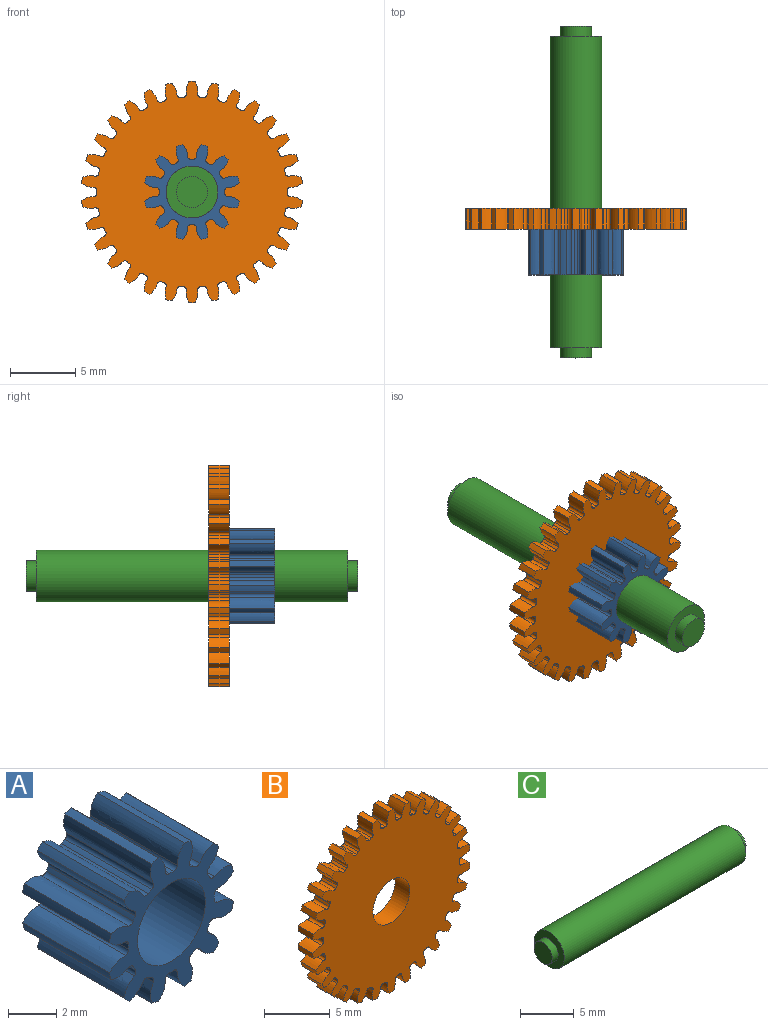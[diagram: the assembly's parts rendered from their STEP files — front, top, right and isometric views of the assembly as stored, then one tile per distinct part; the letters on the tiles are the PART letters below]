
ASSEMBLY  parts=3 mates=2
PART A: 75 faces, bbox 7.3x5.1x7.3 mm
  f0: extruded ~5.08x0.93mm, area 5.4mm2, adj f47,f48,f49,f50
  f1: cylinder r=2.51mm len=5.08mm, axis (0,1,0), area 1.2mm2, adj f48,f49,f50,f51
  f2: extruded ~5.08x0.93mm, area 5.4mm2, adj f3,f48,f49,f51
  f3: cylinder r=3.7mm len=5.08mm, axis (0,1,0), area 2.1mm2, adj f2,f4,f48,f49
  f4: extruded ~5.08x1.01mm, area 5.4mm2, adj f3,f48,f49,f52
  f5: cylinder r=2.51mm len=5.08mm, axis (0,1,0), area 1.2mm2, adj f48,f49,f52,f53
  f6: extruded ~5.08x0.82mm, area 5.4mm2, adj f7,f48,f49,f53
  f7: cylinder r=3.7mm len=5.08mm, axis (0,1,0), area 2.1mm2, adj f6,f8,f48,f49
  f8: extruded ~5.08x0.82mm, area 5.4mm2, adj f7,f48,f49,f54
  f9: cylinder r=2.51mm len=5.08mm, axis (0,1,0), area 1.2mm2, adj f48,f49,f54,f55
  f10: extruded ~5.08x1.01mm, area 5.4mm2, adj f11,f48,f49,f55
  f11: cylinder r=3.7mm len=5.08mm, axis (0,1,0), area 2.1mm2, adj f10,f12,f48,f49
  f12: extruded ~5.08x0.93mm, area 5.4mm2, adj f11,f48,f49,f56
  f13: cylinder r=2.51mm len=5.08mm, axis (0,1,0), area 1.2mm2, adj f48,f49,f56,f57
  f14: extruded ~5.08x0.93mm, area 5.4mm2, adj f15,f48,f49,f57
  f15: cylinder r=3.7mm len=5.08mm, axis (0,1,0), area 2.1mm2, adj f14,f16,f48,f49
  f16: extruded ~5.08x1.01mm, area 5.4mm2, adj f15,f48,f49,f58
  f17: cylinder r=2.51mm len=5.08mm, axis (0,1,0), area 1.2mm2, adj f48,f49,f58,f59
  f18: extruded ~5.08x0.82mm, area 5.4mm2, adj f19,f48,f49,f59
  f19: cylinder r=3.7mm len=5.08mm, axis (0,1,0), area 2.1mm2, adj f18,f20,f48,f49
  f20: extruded ~5.08x0.82mm, area 5.4mm2, adj f19,f48,f49,f60
  f21: cylinder r=2.51mm len=5.08mm, axis (0,1,0), area 1.2mm2, adj f48,f49,f60,f61
  f22: extruded ~5.08x1.01mm, area 5.4mm2, adj f23,f48,f49,f61
  f23: cylinder r=3.7mm len=5.08mm, axis (0,1,0), area 2.1mm2, adj f22,f24,f48,f49
  f24: extruded ~5.08x0.93mm, area 5.4mm2, adj f23,f48,f49,f62
  f25: cylinder r=2.51mm len=5.08mm, axis (0,1,0), area 1.2mm2, adj f48,f49,f62,f63
  f26: extruded ~5.08x0.93mm, area 5.4mm2, adj f27,f48,f49,f63
  f27: cylinder r=3.7mm len=5.08mm, axis (0,1,0), area 2.1mm2, adj f26,f28,f48,f49
  f28: extruded ~5.08x1.01mm, area 5.4mm2, adj f27,f48,f49,f64
  f29: cylinder r=2.51mm len=5.08mm, axis (0,1,0), area 1.2mm2, adj f48,f49,f64,f65
  f30: extruded ~5.08x0.82mm, area 5.4mm2, adj f31,f48,f49,f65
  f31: cylinder r=3.7mm len=5.08mm, axis (0,1,0), area 2.1mm2, adj f30,f32,f48,f49
  f32: extruded ~5.08x0.82mm, area 5.4mm2, adj f31,f48,f49,f66
  f33: cylinder r=2.51mm len=5.08mm, axis (0,1,0), area 1.2mm2, adj f48,f49,f66,f67
  f34: extruded ~5.08x1.01mm, area 5.4mm2, adj f35,f48,f49,f67
  f35: cylinder r=3.7mm len=5.08mm, axis (0,1,0), area 2.1mm2, adj f34,f36,f48,f49
  f36: extruded ~5.08x0.93mm, area 5.4mm2, adj f35,f48,f49,f68
  f37: cylinder r=2.51mm len=5.08mm, axis (0,1,0), area 1.2mm2, adj f48,f49,f68,f69
  f38: extruded ~5.08x0.93mm, area 5.4mm2, adj f39,f48,f49,f69
  f39: cylinder r=3.7mm len=5.08mm, axis (0,1,0), area 2.1mm2, adj f38,f40,f48,f49
  f40: extruded ~5.08x1.01mm, area 5.4mm2, adj f39,f48,f49,f70
  f41: cylinder r=2.51mm len=5.08mm, axis (0,1,0), area 1.2mm2, adj f48,f49,f70,f71
  f42: extruded ~5.08x0.82mm, area 5.4mm2, adj f43,f48,f49,f71
  f43: cylinder r=3.7mm len=5.08mm, axis (0,1,0), area 2.1mm2, adj f42,f44,f48,f49
  f44: extruded ~5.08x0.82mm, area 5.4mm2, adj f43,f48,f49,f72
  f45: cylinder r=2.51mm len=5.08mm, axis (0,1,0), area 1.2mm2, adj f48,f49,f72,f73
  f46: extruded ~5.08x1.01mm, area 5.4mm2, adj f47,f48,f49,f73
  f47: cylinder r=3.7mm len=5.08mm, axis (0,1,0), area 2.1mm2, adj f0,f46,f48,f49
  f48: plane 7.28x7.28mm, normal (0,-1,0), area 18.1mm2, adj f0,f1,f2,f3,f4,f5,f6,f7
  f49: plane 7.28x7.28mm, normal (0,1,0), area 18.1mm2, adj f0,f1,f2,f3,f4,f5,f6,f7
  f50: cylinder r=0.21mm len=5.08mm, axis (0,1,0), area 1.6mm2, adj f0,f1,f48,f49
  f51: cylinder r=0.21mm len=5.08mm, axis (0,1,0), area 1.6mm2, adj f1,f2,f48,f49
  f52: cylinder r=0.21mm len=5.08mm, axis (0,1,0), area 1.6mm2, adj f4,f5,f48,f49
  f53: cylinder r=0.21mm len=5.08mm, axis (0,1,0), area 1.6mm2, adj f5,f6,f48,f49
  f54: cylinder r=0.21mm len=5.08mm, axis (0,1,0), area 1.6mm2, adj f8,f9,f48,f49
  f55: cylinder r=0.21mm len=5.08mm, axis (0,1,0), area 1.6mm2, adj f9,f10,f48,f49
  f56: cylinder r=0.21mm len=5.08mm, axis (0,1,0), area 1.6mm2, adj f12,f13,f48,f49
  f57: cylinder r=0.21mm len=5.08mm, axis (0,1,0), area 1.6mm2, adj f13,f14,f48,f49
  f58: cylinder r=0.21mm len=5.08mm, axis (0,1,0), area 1.6mm2, adj f16,f17,f48,f49
  f59: cylinder r=0.21mm len=5.08mm, axis (0,1,0), area 1.6mm2, adj f17,f18,f48,f49
  f60: cylinder r=0.21mm len=5.08mm, axis (0,1,0), area 1.6mm2, adj f20,f21,f48,f49
  f61: cylinder r=0.21mm len=5.08mm, axis (0,1,0), area 1.6mm2, adj f21,f22,f48,f49
  f62: cylinder r=0.21mm len=5.08mm, axis (0,1,0), area 1.6mm2, adj f24,f25,f48,f49
  f63: cylinder r=0.21mm len=5.08mm, axis (0,1,0), area 1.6mm2, adj f25,f26,f48,f49
  f64: cylinder r=0.21mm len=5.08mm, axis (0,1,0), area 1.6mm2, adj f28,f29,f48,f49
  f65: cylinder r=0.21mm len=5.08mm, axis (0,1,0), area 1.6mm2, adj f29,f30,f48,f49
  f66: cylinder r=0.21mm len=5.08mm, axis (0,1,0), area 1.6mm2, adj f32,f33,f48,f49
  f67: cylinder r=0.21mm len=5.08mm, axis (0,1,0), area 1.6mm2, adj f33,f34,f48,f49
  f68: cylinder r=0.21mm len=5.08mm, axis (0,1,0), area 1.6mm2, adj f36,f37,f48,f49
  f69: cylinder r=0.21mm len=5.08mm, axis (0,1,0), area 1.6mm2, adj f37,f38,f48,f49
  f70: cylinder r=0.21mm len=5.08mm, axis (0,1,0), area 1.6mm2, adj f40,f41,f48,f49
  f71: cylinder r=0.21mm len=5.08mm, axis (0,1,0), area 1.6mm2, adj f41,f42,f48,f49
  f72: cylinder r=0.21mm len=5.08mm, axis (0,1,0), area 1.6mm2, adj f44,f45,f48,f49
  f73: cylinder r=0.21mm len=5.08mm, axis (0,1,0), area 1.6mm2, adj f45,f46,f48,f49
  f74: cylinder r=1.98mm len=5.08mm, axis (0,1,0), area 63.3mm2, adj f48,f49
PART B: 183 faces, bbox 16.9x1.6x16.9 mm
  f0: extruded ~1.59x0.95mm, area 1.6mm2, adj f120,f121,f122,f123
  f1: cylinder r=7.28mm len=1.59mm, axis (0,1,0), area 0.4mm2, adj f121,f122,f123,f124
  f2: extruded ~1.59x0.95mm, area 1.6mm2, adj f3,f121,f122,f124
  f3: cylinder r=8.47mm len=1.59mm, axis (0,1,0), area 0.8mm2, adj f2,f4,f121,f122
  f4: extruded ~1.59x0.99mm, area 1.6mm2, adj f3,f121,f122,f125
  f5: cylinder r=7.28mm len=1.59mm, axis (0,1,0), area 0.4mm2, adj f121,f122,f125,f126
  f6: extruded ~1.59x0.87mm, area 1.6mm2, adj f7,f121,f122,f126
  f7: cylinder r=8.47mm len=1.59mm, axis (0,1,0), area 0.8mm2, adj f6,f8,f121,f122
  f8: extruded ~1.59x0.98mm, area 1.6mm2, adj f7,f121,f122,f127
  f9: cylinder r=7.28mm len=1.59mm, axis (0,1,0), area 0.4mm2, adj f121,f122,f127,f128
  f10: extruded ~1.59x0.75mm, area 1.6mm2, adj f11,f121,f122,f128
  f11: cylinder r=8.47mm len=1.59mm, axis (0,1,0), area 0.8mm2, adj f10,f12,f121,f122
  f12: extruded ~1.59x0.94mm, area 1.6mm2, adj f11,f121,f122,f129
  f13: cylinder r=7.28mm len=1.59mm, axis (0,1,0), area 0.4mm2, adj f121,f122,f129,f130
  f14: extruded ~1.59x0.79mm, area 1.6mm2, adj f15,f121,f122,f130
  f15: cylinder r=8.47mm len=1.59mm, axis (0,1,0), area 0.8mm2, adj f14,f16,f121,f122
  f16: extruded ~1.59x0.85mm, area 1.6mm2, adj f15,f121,f122,f131
  f17: cylinder r=7.28mm len=1.59mm, axis (0,1,0), area 0.4mm2, adj f121,f122,f131,f132
  f18: extruded ~1.59x0.9mm, area 1.6mm2, adj f19,f121,f122,f132
  f19: cylinder r=8.47mm len=1.59mm, axis (0,1,0), area 0.8mm2, adj f18,f20,f121,f122
  f20: extruded ~1.59x0.72mm, area 1.6mm2, adj f19,f121,f122,f133
  f21: cylinder r=7.28mm len=1.59mm, axis (0,1,0), area 0.4mm2, adj f121,f122,f133,f134
  f22: extruded ~1.59x0.96mm, area 1.6mm2, adj f23,f121,f122,f134
  f23: cylinder r=8.47mm len=1.59mm, axis (0,1,0), area 0.8mm2, adj f22,f24,f121,f122
  f24: extruded ~1.59x0.81mm, area 1.6mm2, adj f23,f121,f122,f135
  f25: cylinder r=7.28mm len=1.59mm, axis (0,1,0), area 0.4mm2, adj f121,f122,f135,f136
  f26: extruded ~1.59x0.99mm, area 1.6mm2, adj f27,f121,f122,f136
  f27: cylinder r=8.47mm len=1.59mm, axis (0,1,0), area 0.8mm2, adj f26,f28,f121,f122
  f28: extruded ~1.59x0.91mm, area 1.6mm2, adj f27,f121,f122,f137
  f29: cylinder r=7.28mm len=1.59mm, axis (0,1,0), area 0.4mm2, adj f121,f122,f137,f138
  f30: extruded ~1.59x0.97mm, area 1.6mm2, adj f31,f121,f122,f138
  f31: cylinder r=8.47mm len=1.59mm, axis (0,1,0), area 0.8mm2, adj f30,f32,f121,f122
  f32: extruded ~1.59x0.97mm, area 1.6mm2, adj f31,f121,f122,f139
  f33: cylinder r=7.28mm len=1.59mm, axis (0,1,0), area 0.4mm2, adj f121,f122,f139,f140
  f34: extruded ~1.59x0.91mm, area 1.6mm2, adj f35,f121,f122,f140
  f35: cylinder r=8.47mm len=1.59mm, axis (0,1,0), area 0.8mm2, adj f34,f36,f121,f122
  f36: extruded ~1.59x0.99mm, area 1.6mm2, adj f35,f121,f122,f141
  f37: cylinder r=7.28mm len=1.59mm, axis (0,1,0), area 0.4mm2, adj f121,f122,f141,f142
  f38: extruded ~1.59x0.81mm, area 1.6mm2, adj f39,f121,f122,f142
  f39: cylinder r=8.47mm len=1.59mm, axis (0,1,0), area 0.8mm2, adj f38,f40,f121,f122
  f40: extruded ~1.59x0.96mm, area 1.6mm2, adj f39,f121,f122,f143
  f41: cylinder r=7.28mm len=1.59mm, axis (0,1,0), area 0.4mm2, adj f121,f122,f143,f144
  f42: extruded ~1.59x0.72mm, area 1.6mm2, adj f43,f121,f122,f144
  f43: cylinder r=8.47mm len=1.59mm, axis (0,1,0), area 0.8mm2, adj f42,f44,f121,f122
  f44: extruded ~1.59x0.9mm, area 1.6mm2, adj f43,f121,f122,f145
  f45: cylinder r=7.28mm len=1.59mm, axis (0,1,0), area 0.4mm2, adj f121,f122,f145,f146
  f46: extruded ~1.59x0.85mm, area 1.6mm2, adj f47,f121,f122,f146
  f47: cylinder r=8.47mm len=1.59mm, axis (0,1,0), area 0.8mm2, adj f46,f48,f121,f122
  f48: extruded ~1.59x0.79mm, area 1.6mm2, adj f47,f121,f122,f147
  f49: cylinder r=7.28mm len=1.59mm, axis (0,1,0), area 0.4mm2, adj f121,f122,f147,f148
  f50: extruded ~1.59x0.94mm, area 1.6mm2, adj f51,f121,f122,f148
  f51: cylinder r=8.47mm len=1.59mm, axis (0,1,0), area 0.8mm2, adj f50,f52,f121,f122
  f52: extruded ~1.59x0.75mm, area 1.6mm2, adj f51,f121,f122,f149
  f53: cylinder r=7.28mm len=1.59mm, axis (0,1,0), area 0.4mm2, adj f121,f122,f149,f150
  f54: extruded ~1.59x0.98mm, area 1.6mm2, adj f55,f121,f122,f150
  f55: cylinder r=8.47mm len=1.59mm, axis (0,1,0), area 0.8mm2, adj f54,f56,f121,f122
  f56: extruded ~1.59x0.87mm, area 1.6mm2, adj f55,f121,f122,f151
  f57: cylinder r=7.28mm len=1.59mm, axis (0,1,0), area 0.4mm2, adj f121,f122,f151,f152
  f58: extruded ~1.59x0.99mm, area 1.6mm2, adj f59,f121,f122,f152
  f59: cylinder r=8.47mm len=1.59mm, axis (0,1,0), area 0.8mm2, adj f58,f60,f121,f122
  f60: extruded ~1.59x0.95mm, area 1.6mm2, adj f59,f121,f122,f153
  f61: cylinder r=7.28mm len=1.59mm, axis (0,1,0), area 0.4mm2, adj f121,f122,f153,f154
  f62: extruded ~1.59x0.95mm, area 1.6mm2, adj f63,f121,f122,f154
  f63: cylinder r=8.47mm len=1.59mm, axis (0,1,0), area 0.8mm2, adj f62,f64,f121,f122
  f64: extruded ~1.59x0.99mm, area 1.6mm2, adj f63,f121,f122,f155
  f65: cylinder r=7.28mm len=1.59mm, axis (0,1,0), area 0.4mm2, adj f121,f122,f155,f156
  f66: extruded ~1.59x0.87mm, area 1.6mm2, adj f67,f121,f122,f156
  f67: cylinder r=8.47mm len=1.59mm, axis (0,1,0), area 0.8mm2, adj f66,f68,f121,f122
  f68: extruded ~1.59x0.98mm, area 1.6mm2, adj f67,f121,f122,f157
  f69: cylinder r=7.28mm len=1.59mm, axis (0,1,0), area 0.4mm2, adj f121,f122,f157,f158
  f70: extruded ~1.59x0.75mm, area 1.6mm2, adj f71,f121,f122,f158
  f71: cylinder r=8.47mm len=1.59mm, axis (0,1,0), area 0.8mm2, adj f70,f72,f121,f122
  f72: extruded ~1.59x0.94mm, area 1.6mm2, adj f71,f121,f122,f159
  f73: cylinder r=7.28mm len=1.59mm, axis (0,1,0), area 0.4mm2, adj f121,f122,f159,f160
  f74: extruded ~1.59x0.79mm, area 1.6mm2, adj f75,f121,f122,f160
  f75: cylinder r=8.47mm len=1.59mm, axis (0,1,0), area 0.8mm2, adj f74,f76,f121,f122
  f76: extruded ~1.59x0.85mm, area 1.6mm2, adj f75,f121,f122,f161
  f77: cylinder r=7.28mm len=1.59mm, axis (0,1,0), area 0.4mm2, adj f121,f122,f161,f162
  f78: extruded ~1.59x0.9mm, area 1.6mm2, adj f79,f121,f122,f162
  f79: cylinder r=8.47mm len=1.59mm, axis (0,1,0), area 0.8mm2, adj f78,f80,f121,f122
  f80: extruded ~1.59x0.72mm, area 1.6mm2, adj f79,f121,f122,f163
  f81: cylinder r=7.28mm len=1.59mm, axis (0,1,0), area 0.4mm2, adj f121,f122,f163,f164
  f82: extruded ~1.59x0.96mm, area 1.6mm2, adj f83,f121,f122,f164
  f83: cylinder r=8.47mm len=1.59mm, axis (0,1,0), area 0.8mm2, adj f82,f84,f121,f122
  f84: extruded ~1.59x0.81mm, area 1.6mm2, adj f83,f121,f122,f165
  f85: cylinder r=7.28mm len=1.59mm, axis (0,1,0), area 0.4mm2, adj f121,f122,f165,f166
  f86: extruded ~1.59x0.99mm, area 1.6mm2, adj f87,f121,f122,f166
  f87: cylinder r=8.47mm len=1.59mm, axis (0,1,0), area 0.8mm2, adj f86,f88,f121,f122
  f88: extruded ~1.59x0.91mm, area 1.6mm2, adj f87,f121,f122,f167
  f89: cylinder r=7.28mm len=1.59mm, axis (0,1,0), area 0.4mm2, adj f121,f122,f167,f168
  f90: extruded ~1.59x0.97mm, area 1.6mm2, adj f91,f121,f122,f168
  f91: cylinder r=8.47mm len=1.59mm, axis (0,1,0), area 0.8mm2, adj f90,f92,f121,f122
  f92: extruded ~1.59x0.97mm, area 1.6mm2, adj f91,f121,f122,f169
  f93: cylinder r=7.28mm len=1.59mm, axis (0,1,0), area 0.4mm2, adj f121,f122,f169,f170
  f94: extruded ~1.59x0.91mm, area 1.6mm2, adj f95,f121,f122,f170
  f95: cylinder r=8.47mm len=1.59mm, axis (0,1,0), area 0.8mm2, adj f94,f96,f121,f122
  f96: extruded ~1.59x0.99mm, area 1.6mm2, adj f95,f121,f122,f171
  f97: cylinder r=7.28mm len=1.59mm, axis (0,1,0), area 0.4mm2, adj f121,f122,f171,f172
  f98: extruded ~1.59x0.81mm, area 1.6mm2, adj f99,f121,f122,f172
  f99: cylinder r=8.47mm len=1.59mm, axis (0,1,0), area 0.8mm2, adj f98,f100,f121,f122
  f100: extruded ~1.59x0.96mm, area 1.6mm2, adj f99,f121,f122,f173
  f101: cylinder r=7.28mm len=1.59mm, axis (0,1,0), area 0.4mm2, adj f121,f122,f173,f174
  f102: extruded ~1.59x0.72mm, area 1.6mm2, adj f103,f121,f122,f174
  f103: cylinder r=8.47mm len=1.59mm, axis (0,1,0), area 0.8mm2, adj f102,f104,f121,f122
  f104: extruded ~1.59x0.9mm, area 1.6mm2, adj f103,f121,f122,f175
  f105: cylinder r=7.28mm len=1.59mm, axis (0,1,0), area 0.4mm2, adj f121,f122,f175,f176
  f106: extruded ~1.59x0.85mm, area 1.6mm2, adj f107,f121,f122,f176
  f107: cylinder r=8.47mm len=1.59mm, axis (0,1,0), area 0.8mm2, adj f106,f108,f121,f122
  f108: extruded ~1.59x0.79mm, area 1.6mm2, adj f107,f121,f122,f177
  f109: cylinder r=7.28mm len=1.59mm, axis (0,1,0), area 0.4mm2, adj f121,f122,f177,f178
  f110: extruded ~1.59x0.94mm, area 1.6mm2, adj f111,f121,f122,f178
  f111: cylinder r=8.47mm len=1.59mm, axis (0,1,0), area 0.8mm2, adj f110,f112,f121,f122
  f112: extruded ~1.59x0.75mm, area 1.6mm2, adj f111,f121,f122,f179
  f113: cylinder r=7.28mm len=1.59mm, axis (0,1,0), area 0.4mm2, adj f121,f122,f179,f180
  f114: extruded ~1.59x0.98mm, area 1.6mm2, adj f115,f121,f122,f180
  f115: cylinder r=8.47mm len=1.59mm, axis (0,1,0), area 0.8mm2, adj f114,f116,f121,f122
  f116: extruded ~1.59x0.87mm, area 1.6mm2, adj f115,f121,f122,f181
  f117: cylinder r=7.28mm len=1.59mm, axis (0,1,0), area 0.4mm2, adj f121,f122,f181,f182
  f118: extruded ~1.59x0.99mm, area 1.6mm2, adj f120,f121,f122,f182
  f119: cylinder r=1.98mm len=3.97mm, axis (0,1,0), area 19.8mm2, adj f121,f122
  f120: cylinder r=8.47mm len=1.59mm, axis (0,1,0), area 0.8mm2, adj f0,f118,f121,f122
  f121: plane 16.94x16.9mm, normal (0,-1,0), area 182.5mm2, adj f0,f1,f2,f3,f4,f5,f6,f7
  f122: plane 16.94x16.9mm, normal (0,1,0), area 182.5mm2, adj f0,f1,f2,f3,f4,f5,f6,f7
  f123: cylinder r=0.23mm len=1.59mm, axis (0,1,0), area 0.6mm2, adj f0,f1,f121,f122
  f124: cylinder r=0.23mm len=1.59mm, axis (0,1,0), area 0.6mm2, adj f1,f2,f121,f122
  f125: cylinder r=0.23mm len=1.59mm, axis (0,1,0), area 0.6mm2, adj f4,f5,f121,f122
  f126: cylinder r=0.23mm len=1.59mm, axis (0,1,0), area 0.6mm2, adj f5,f6,f121,f122
  f127: cylinder r=0.23mm len=1.59mm, axis (0,1,0), area 0.6mm2, adj f8,f9,f121,f122
  f128: cylinder r=0.23mm len=1.59mm, axis (0,1,0), area 0.6mm2, adj f9,f10,f121,f122
  f129: cylinder r=0.23mm len=1.59mm, axis (0,1,0), area 0.6mm2, adj f12,f13,f121,f122
  f130: cylinder r=0.23mm len=1.59mm, axis (0,1,0), area 0.6mm2, adj f13,f14,f121,f122
  f131: cylinder r=0.23mm len=1.59mm, axis (0,1,0), area 0.6mm2, adj f16,f17,f121,f122
  f132: cylinder r=0.23mm len=1.59mm, axis (0,1,0), area 0.6mm2, adj f17,f18,f121,f122
  f133: cylinder r=0.23mm len=1.59mm, axis (0,1,0), area 0.6mm2, adj f20,f21,f121,f122
  f134: cylinder r=0.23mm len=1.59mm, axis (0,1,0), area 0.6mm2, adj f21,f22,f121,f122
  f135: cylinder r=0.23mm len=1.59mm, axis (0,1,0), area 0.6mm2, adj f24,f25,f121,f122
  f136: cylinder r=0.23mm len=1.59mm, axis (0,1,0), area 0.6mm2, adj f25,f26,f121,f122
  f137: cylinder r=0.23mm len=1.59mm, axis (0,1,0), area 0.6mm2, adj f28,f29,f121,f122
  f138: cylinder r=0.23mm len=1.59mm, axis (0,1,0), area 0.6mm2, adj f29,f30,f121,f122
  f139: cylinder r=0.23mm len=1.59mm, axis (0,1,0), area 0.6mm2, adj f32,f33,f121,f122
  f140: cylinder r=0.23mm len=1.59mm, axis (0,1,0), area 0.6mm2, adj f33,f34,f121,f122
  f141: cylinder r=0.23mm len=1.59mm, axis (0,1,0), area 0.6mm2, adj f36,f37,f121,f122
  f142: cylinder r=0.23mm len=1.59mm, axis (0,1,0), area 0.6mm2, adj f37,f38,f121,f122
  f143: cylinder r=0.23mm len=1.59mm, axis (0,1,0), area 0.6mm2, adj f40,f41,f121,f122
  f144: cylinder r=0.23mm len=1.59mm, axis (0,1,0), area 0.6mm2, adj f41,f42,f121,f122
  f145: cylinder r=0.23mm len=1.59mm, axis (0,1,0), area 0.6mm2, adj f44,f45,f121,f122
  f146: cylinder r=0.23mm len=1.59mm, axis (0,1,0), area 0.6mm2, adj f45,f46,f121,f122
  f147: cylinder r=0.23mm len=1.59mm, axis (0,1,0), area 0.6mm2, adj f48,f49,f121,f122
  f148: cylinder r=0.23mm len=1.59mm, axis (0,1,0), area 0.6mm2, adj f49,f50,f121,f122
  f149: cylinder r=0.23mm len=1.59mm, axis (0,1,0), area 0.6mm2, adj f52,f53,f121,f122
  f150: cylinder r=0.23mm len=1.59mm, axis (0,1,0), area 0.6mm2, adj f53,f54,f121,f122
  f151: cylinder r=0.23mm len=1.59mm, axis (0,1,0), area 0.6mm2, adj f56,f57,f121,f122
  f152: cylinder r=0.23mm len=1.59mm, axis (0,1,0), area 0.6mm2, adj f57,f58,f121,f122
  f153: cylinder r=0.23mm len=1.59mm, axis (0,1,0), area 0.6mm2, adj f60,f61,f121,f122
  f154: cylinder r=0.23mm len=1.59mm, axis (0,1,0), area 0.6mm2, adj f61,f62,f121,f122
  f155: cylinder r=0.23mm len=1.59mm, axis (0,1,0), area 0.6mm2, adj f64,f65,f121,f122
  f156: cylinder r=0.23mm len=1.59mm, axis (0,1,0), area 0.6mm2, adj f65,f66,f121,f122
  f157: cylinder r=0.23mm len=1.59mm, axis (0,1,0), area 0.6mm2, adj f68,f69,f121,f122
  f158: cylinder r=0.23mm len=1.59mm, axis (0,1,0), area 0.6mm2, adj f69,f70,f121,f122
  f159: cylinder r=0.23mm len=1.59mm, axis (0,1,0), area 0.6mm2, adj f72,f73,f121,f122
  f160: cylinder r=0.23mm len=1.59mm, axis (0,1,0), area 0.6mm2, adj f73,f74,f121,f122
  f161: cylinder r=0.23mm len=1.59mm, axis (0,1,0), area 0.6mm2, adj f76,f77,f121,f122
  f162: cylinder r=0.23mm len=1.59mm, axis (0,1,0), area 0.6mm2, adj f77,f78,f121,f122
  f163: cylinder r=0.23mm len=1.59mm, axis (0,1,0), area 0.6mm2, adj f80,f81,f121,f122
  f164: cylinder r=0.23mm len=1.59mm, axis (0,1,0), area 0.6mm2, adj f81,f82,f121,f122
  f165: cylinder r=0.23mm len=1.59mm, axis (0,1,0), area 0.6mm2, adj f84,f85,f121,f122
  f166: cylinder r=0.23mm len=1.59mm, axis (0,1,0), area 0.6mm2, adj f85,f86,f121,f122
  f167: cylinder r=0.23mm len=1.59mm, axis (0,1,0), area 0.6mm2, adj f88,f89,f121,f122
  f168: cylinder r=0.23mm len=1.59mm, axis (0,1,0), area 0.6mm2, adj f89,f90,f121,f122
  f169: cylinder r=0.23mm len=1.59mm, axis (0,1,0), area 0.6mm2, adj f92,f93,f121,f122
  f170: cylinder r=0.23mm len=1.59mm, axis (0,1,0), area 0.6mm2, adj f93,f94,f121,f122
  f171: cylinder r=0.23mm len=1.59mm, axis (0,1,0), area 0.6mm2, adj f96,f97,f121,f122
  f172: cylinder r=0.23mm len=1.59mm, axis (0,1,0), area 0.6mm2, adj f97,f98,f121,f122
  f173: cylinder r=0.23mm len=1.59mm, axis (0,1,0), area 0.6mm2, adj f100,f101,f121,f122
  f174: cylinder r=0.23mm len=1.59mm, axis (0,1,0), area 0.6mm2, adj f101,f102,f121,f122
  f175: cylinder r=0.23mm len=1.59mm, axis (0,1,0), area 0.6mm2, adj f104,f105,f121,f122
  f176: cylinder r=0.23mm len=1.59mm, axis (0,1,0), area 0.6mm2, adj f105,f106,f121,f122
  f177: cylinder r=0.23mm len=1.59mm, axis (0,1,0), area 0.6mm2, adj f108,f109,f121,f122
  f178: cylinder r=0.23mm len=1.59mm, axis (0,1,0), area 0.6mm2, adj f109,f110,f121,f122
  f179: cylinder r=0.23mm len=1.59mm, axis (0,1,0), area 0.6mm2, adj f112,f113,f121,f122
  f180: cylinder r=0.23mm len=1.59mm, axis (0,1,0), area 0.6mm2, adj f113,f114,f121,f122
  f181: cylinder r=0.23mm len=1.59mm, axis (0,1,0), area 0.6mm2, adj f116,f117,f121,f122
  f182: cylinder r=0.23mm len=1.59mm, axis (0,1,0), area 0.6mm2, adj f117,f118,f121,f122
PART C: 7 faces, bbox 25.4x4x4 mm
  f0: cylinder r=1.19mm len=2.38mm, axis (-1,0,0), area 5.9mm2, adj f1,f3
  f1: plane 2.38x2.38mm, normal (1,0,0), area 4.5mm2, adj f0
  f2: cylinder r=1.98mm len=23.81mm, axis (-1,0,0), area 296.9mm2, adj f3,f4
  f3: plane 3.97x3.97mm, normal (1,0,0), area 7.9mm2, adj f0,f2
  f4: plane 3.97x3.97mm, normal (-1,0,0), area 7.9mm2, adj f2,f6
  f5: plane 2.38x2.38mm, normal (-1,0,0), area 4.5mm2, adj f6
  f6: cylinder r=1.19mm len=2.38mm, axis (-1,0,0), area 5.9mm2, adj f4,f5
PLACE A t=(-10.58,-6.63,-1.98)mm
PLACE B t=(-10.58,-6.63,-1.98)mm
PLACE C rot(axis=(0.58,-0.58,-0.58),120deg) t=(-10.58,7.34,-1.98)mm
MATE fastened A.f74 <-> C.f0  axis (0,1,0) through (-10.58,-11.71,-1.98)mm
MATE fastened A.f74 <-> B.f113  axis (0,-1,0) through (-10.58,-11.71,-1.98)mm
